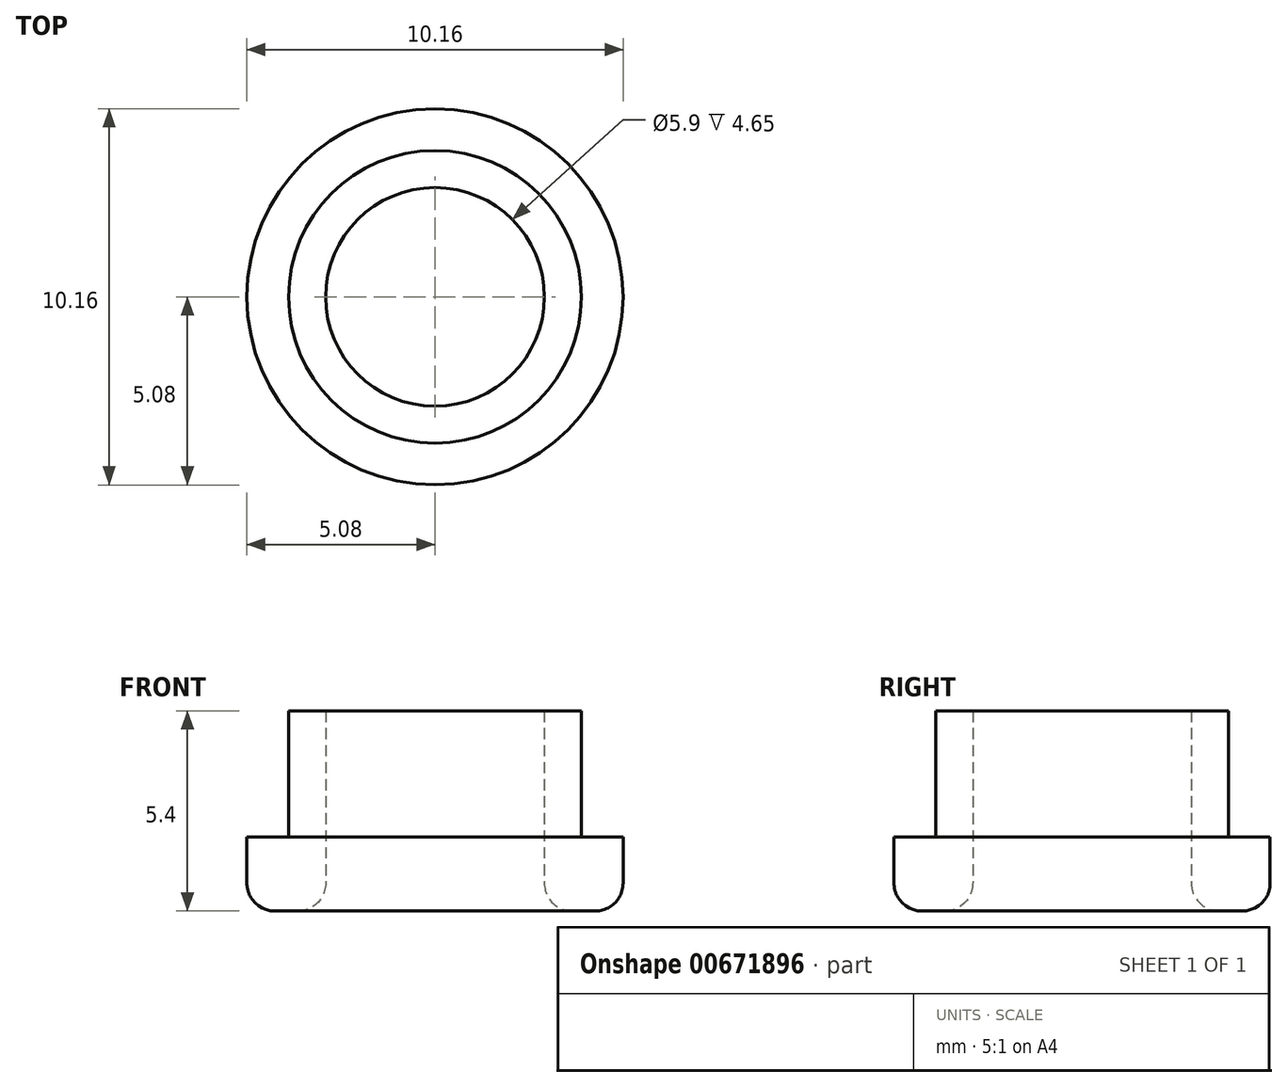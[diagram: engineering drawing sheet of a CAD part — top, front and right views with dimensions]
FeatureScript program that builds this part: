
annotation { "Feature Type Name" : "Feature", "Feature Type Description" : "" }
export const myFeature = defineFeature(function(context is Context, id is Id, definition is map)
    precondition{}
    {
        {
            var Q0;
            Q0=qCreatedBy(makeId("Top.planeOp"),FACE);
            var sketch = newSketch(context, id + "F0", { "sketchPlane" : qUnion([Q0])});
            skCircle(sketch, "E0", {"center": v(0, 0) * mm, "radius": 2.95 * mm});
            skCircle(sketch, "E1", {"center": v(0, 0) * mm, "radius": 3.95 * mm});
            skCircle(sketch, "E2", {"center": v(0, 0) * mm, "radius": 5.08 * mm});
            skSolve(sketch);
        }
        {
            var Q0;
            Q0=makeQuery(id+"F0.imprint","IMPRINT",FACE,{"disambiguationData":[TD([[makeQuery(id+"F0.imprint","IMPRINT",EDGE,{"derivedFrom":sQuery(id+"F0.wireOp",EDGE,"E0")}),-1.0]])]});
            extrude(context, id + "F1", {"entities" : qUnion([Q0]), "depth" : 5.4 * mm, "offsetDistance" : 25 * mm});
        }
        {
            var Q0;
            Q0=makeQuery(id+"F0.imprint","IMPRINT",FACE,{"disambiguationData":[TD([[makeQuery(id+"F0.imprint","IMPRINT",EDGE,{"derivedFrom":sQuery(id+"F0.wireOp",EDGE,"E1")}),-1.0]])]});
            extrude(context, id + "F2", {"entities" : qUnion([Q0]), "operationType" : NewBodyOperationType.ADD, "depth" : 2 * mm, "offsetDistance" : 25 * mm});
        }
        {
            var Q0;
            Q0=makeQuery(id+"F2.opExtrude","CAP_EDGE",EDGE,{"disambiguationData":[OSD([sQuery(id+"F0.wireOp",EDGE,"E2")])],"isStart":true});
            var Q1;
            Q1=makeQuery(id+"F1.opExtrude","CAP_EDGE",EDGE,{"disambiguationData":[OSD([sQuery(id+"F0.wireOp",EDGE,"E0")])],"isStart":true});
            fillet(context, id + "F3", {"entities" : qUnion([Q0, Q1]), "radius" : .75 * mm, "tangentPropagation" : true, "allowEdgeOverflow" : false});
        }
    });
